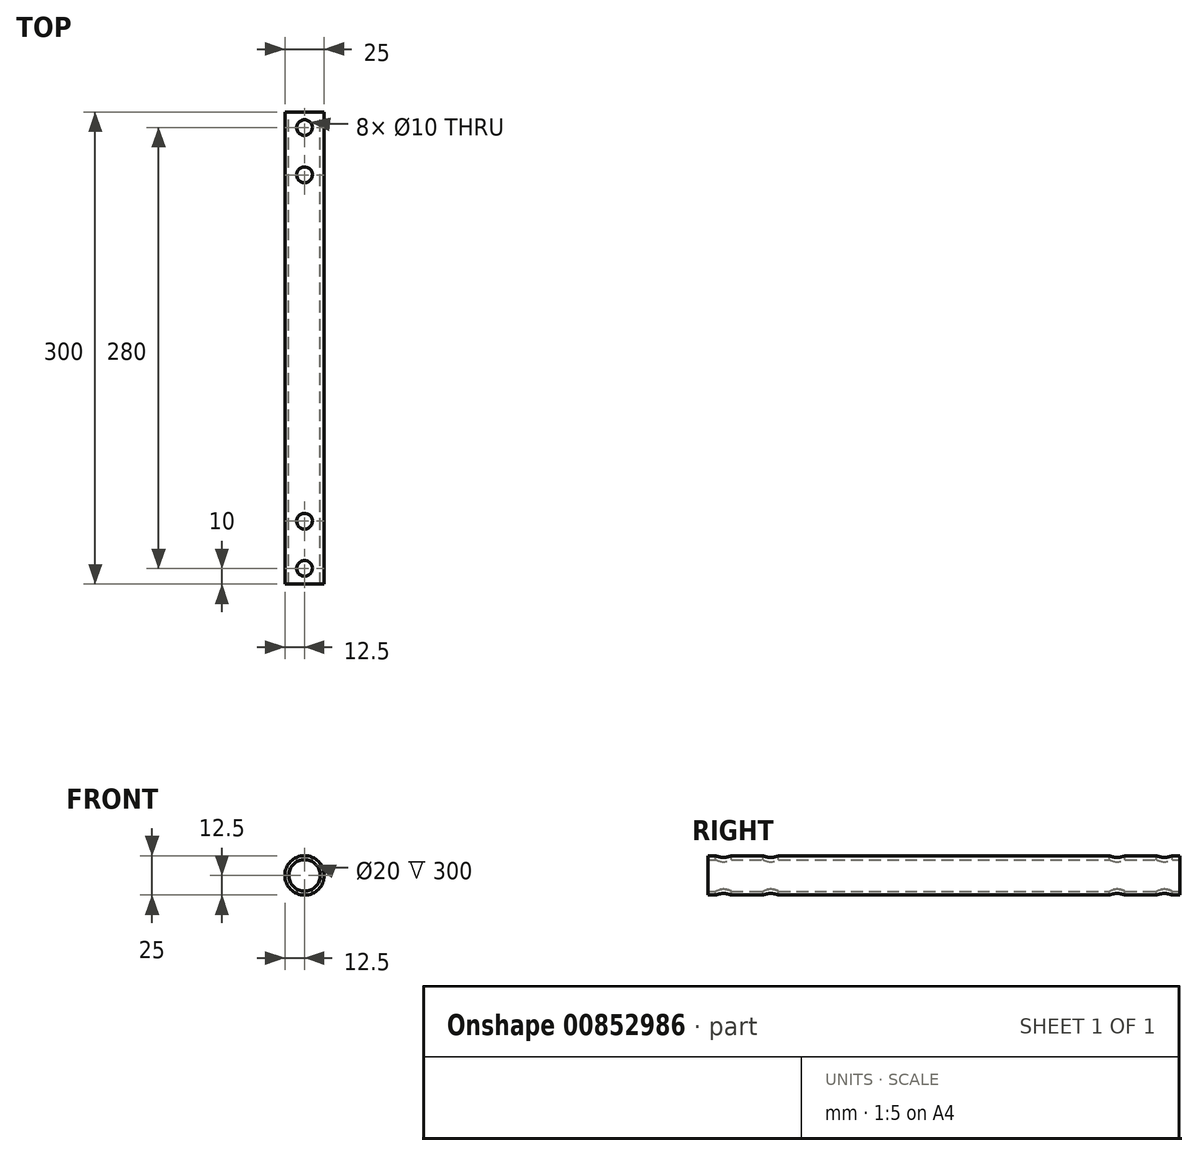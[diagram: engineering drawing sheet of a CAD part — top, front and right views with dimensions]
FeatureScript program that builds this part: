
annotation { "Feature Type Name" : "Feature", "Feature Type Description" : "" }
export const myFeature = defineFeature(function(context is Context, id is Id, definition is map)
    precondition{}
    {
        {
            var Q0;
            Q0=qCreatedBy(makeId("Front.planeOp"),FACE);
            var sketch = newSketch(context, id + "F0", { "sketchPlane" : qUnion([Q0])});
            skCircle(sketch, "E0", {"center": v(0, 0) * mm, "radius": 10 * mm});
            skCircle(sketch, "E1", {"center": v(0, 0) * mm, "radius": 12.5 * mm});
            skSolve(sketch);
        }
        {
            var Q0;
            Q0=makeQuery(id+"F0.imprint","IMPRINT",FACE,{"disambiguationData":[TD([[makeQuery(id+"F0.imprint","IMPRINT",EDGE,{"derivedFrom":sQuery(id+"F0.wireOp",EDGE,"E0")}),-1.0]])]});
            extrude(context, id + "F1", {"entities" : qUnion([Q0]), "depth" : 300 * mm, "offsetDistance" : 25 * mm});
        }
        {
            var Q0;
            Q0=qCreatedBy(makeId("Top.planeOp"),FACE);
            var sketch = newSketch(context, id + "F2", { "sketchPlane" : qUnion([Q0])});
            skLineSegment(sketch, "E2", {"start": v(0, 0) * mm, "end": v(0, -290) * mm, "construction": true});
            skCircle(sketch, "E3", {"center": v(0, -290) * mm, "radius": 5 * mm});
            skLineSegment(sketch, "E4", {"start": v(0, 0) * mm, "end": v(0, -10) * mm, "construction": true});
            skCircle(sketch, "E5", {"center": v(0, -10) * mm, "radius": 5 * mm});
            skLineSegment(sketch, "E6", {"start": v(0, -10) * mm, "end": v(0, -40) * mm});
            skCircle(sketch, "E7", {"center": v(0, -40) * mm, "radius": 5 * mm});
            skCircle(sketch, "E8", {"center": v(0, -10) * mm, "radius": 15 * mm});
            skLineSegment(sketch, "E9", {"start": v(0, -290) * mm, "end": v(0, -260) * mm, "construction": true});
            skCircle(sketch, "E10", {"center": v(0, -260) * mm, "radius": 5 * mm});
            skSolve(sketch);
        }
        {
            var Q0;
            Q0=makeQuery(id+"F2.imprint","IMPRINT",FACE,{"disambiguationData":[TD([[makeQuery(id+"F2.imprint","IMPRINT",EDGE,{"derivedFrom":sQuery(id+"F2.wireOp",EDGE,"E3")}),1.0]])]});
            var Q1;
            Q1=makeQuery(id+"F2.imprint","IMPRINT",FACE,{"disambiguationData":[TD([[makeQuery(id+"F2.imprint","IMPRINT",EDGE,{"derivedFrom":sQuery(id+"F2.wireOp",EDGE,"E5")}),1.0]])]});
            var Q2;
            Q2=makeQuery(id+"F2.imprint","IMPRINT",FACE,{"disambiguationData":[TD([[makeQuery(id+"F2.imprint","IMPRINT",EDGE,{"derivedFrom":sQuery(id+"F2.wireOp",EDGE,"E7")}),1.0]])]});
            var Q3;
            Q3=makeQuery(id+"F2.imprint","IMPRINT",FACE,{"disambiguationData":[TD([[makeQuery(id+"F2.imprint","IMPRINT",EDGE,{"derivedFrom":sQuery(id+"F2.wireOp",EDGE,"E10")}),1.0]])]});
            extrude(context, id + "F3", {"entities" : qUnion([Q0, Q1, Q2, Q3]), "operationType" : NewBodyOperationType.REMOVE, "endBound" : BoundingType.SYMMETRIC, "oppositeDirection" : true, "depth" : 98 * mm, "offsetDistance" : 25 * mm});
        }
    });
